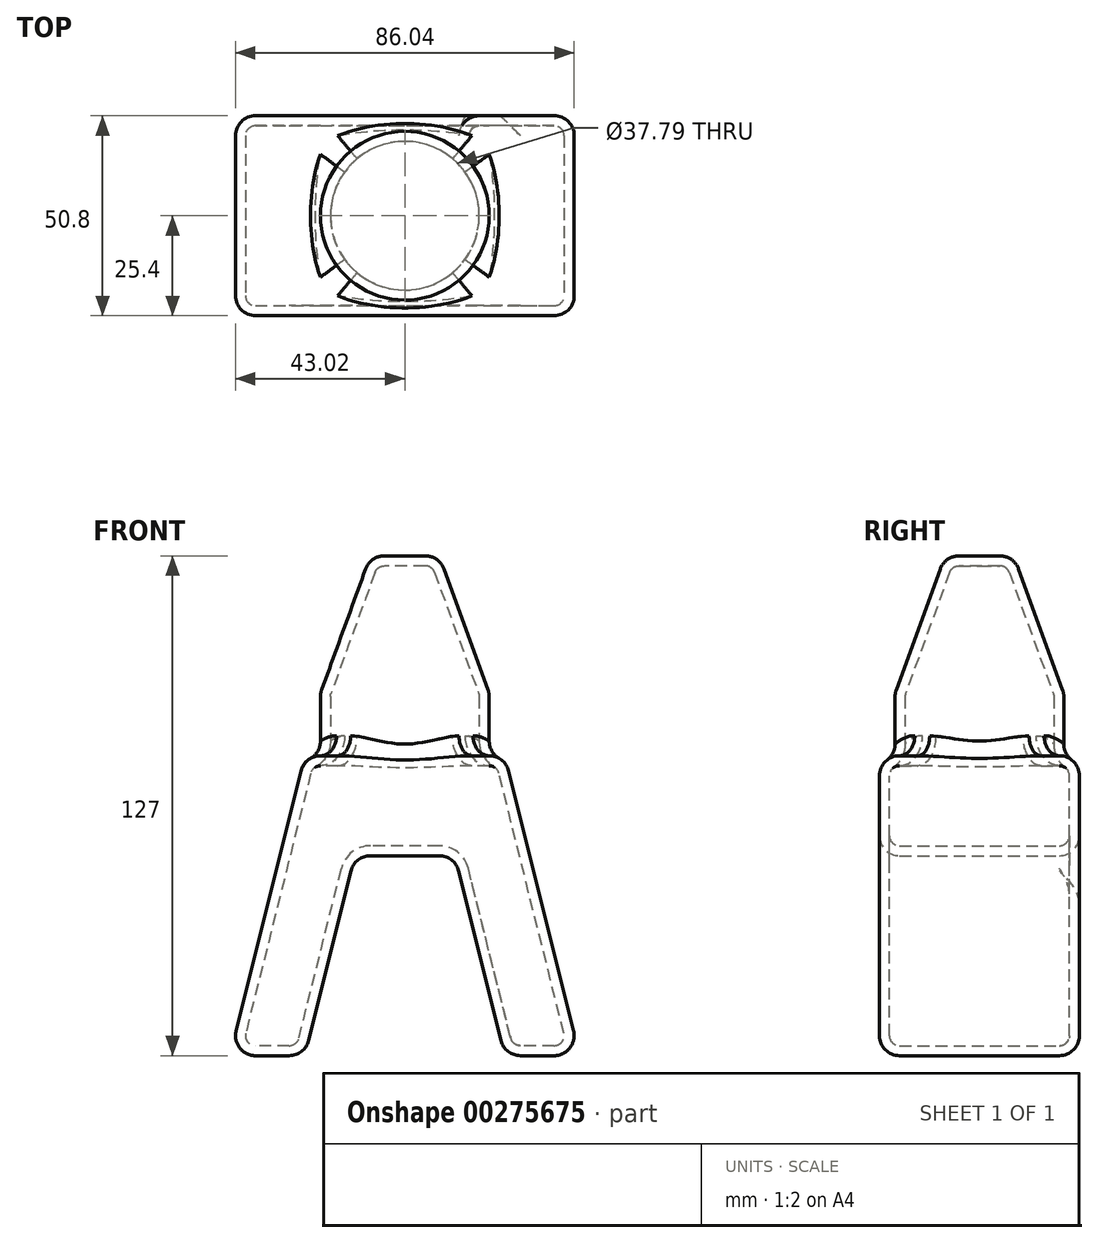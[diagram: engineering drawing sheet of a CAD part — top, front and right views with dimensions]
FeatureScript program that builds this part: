
annotation { "Feature Type Name" : "Feature", "Feature Type Description" : "" }
export const myFeature = defineFeature(function(context is Context, id is Id, definition is map)
    precondition{}
    {
        {
            var Q0;
            Q0=qCreatedBy(makeId("Front.planeOp"),FACE);
            var sketch = newSketch(context, id + "F0", { "sketchPlane" : qUnion([Q0])});
            skLineSegment(sketch, "E0", {"start": v(-25.4, 0) * mm, "end": v(-12.7, 50.8) * mm});
            skLineSegment(sketch, "E1", {"start": v(44.45, 0) * mm, "end": v(25.4, 0) * mm});
            skLineSegment(sketch, "E2", {"start": v(44.45, 0) * mm, "end": v(25.4, 76.2) * mm});
            skLineSegment(sketch, "E3", {"start": v(25.4, 76.2) * mm, "end": v(-25.4, 76.2) * mm});
            skLineSegment(sketch, "E4", {"start": v(-25.4, 76.2) * mm, "end": v(-44.45, 0) * mm});
            skLineSegment(sketch, "E5", {"start": v(-25.4, 0) * mm, "end": v(-44.45, 0) * mm});
            skLineSegment(sketch, "E6", {"start": v(25.4, 0) * mm, "end": v(12.7, 50.8) * mm});
            skLineSegment(sketch, "E7", {"start": v(12.7, 50.8) * mm, "end": v(-12.7, 50.8) * mm});
            skPoint(sketch, "E8", {"position": v(0, 76.2) * mm});
            skPoint(sketch, "E9", {"position": v(0, 50.8) * mm});
            skLineSegment(sketch, "E10", {"start": v(0, 76.2) * mm, "end": v(0, 50.8) * mm, "construction": true});
            skSolve(sketch);
        }
        {
            var Q0;
            Q0 = qSketchRegion(id + "F0", true);
            extrude(context, id + "F1", {"entities" : qUnion([Q0]), "depth" : 25.4 * mm, "hasSecondDirection" : true, "secondDirectionOppositeDirection" : true, "secondDirectionDepth" : 25.4 * mm});
        }
        {
            var Q0;
            Q0=makeQuery(id+"F1.opExtrude","CAP_FACE",FACE,{"disambiguationData":[OSD([sQuery(id+"F0.wireOp",EDGE,"E0"),sQuery(id+"F0.wireOp",EDGE,"E1"),sQuery(id+"F0.wireOp",EDGE,"E2"),sQuery(id+"F0.wireOp",EDGE,"E3"),sQuery(id+"F0.wireOp",EDGE,"E4"),sQuery(id+"F0.wireOp",EDGE,"E5"),sQuery(id+"F0.wireOp",EDGE,"E6"),sQuery(id+"F0.wireOp",EDGE,"E7")])],"isStart":false});
            var Q1;
            Q1=makeQuery(id+"F1.opExtrude","SWEPT_FACE",FACE,{"disambiguationData":[OSD([sQuery(id+"F0.wireOp",EDGE,"E2")])]});
            var Q2;
            Q2=makeQuery(id+"F1.opExtrude","SWEPT_FACE",FACE,{"disambiguationData":[OSD([sQuery(id+"F0.wireOp",EDGE,"E3")])]});
            var Q3;
            Q3=makeQuery(id+"F1.opExtrude","SWEPT_FACE",FACE,{"disambiguationData":[OSD([sQuery(id+"F0.wireOp",EDGE,"E0")])]});
            var Q4;
            Q4=makeQuery(id+"F1.opExtrude","SWEPT_FACE",FACE,{"disambiguationData":[OSD([sQuery(id+"F0.wireOp",EDGE,"E7")])]});
            var Q5;
            Q5=makeQuery(id+"F1.opExtrude","SWEPT_FACE",FACE,{"disambiguationData":[OSD([sQuery(id+"F0.wireOp",EDGE,"E1")])]});
            var Q6;
            Q6=makeQuery(id+"F1.opExtrude","SWEPT_FACE",FACE,{"disambiguationData":[OSD([sQuery(id+"F0.wireOp",EDGE,"E5")])]});
            var Q7;
            Q7=makeQuery(id+"F1.opExtrude","SWEPT_FACE",FACE,{"disambiguationData":[OSD([sQuery(id+"F0.wireOp",EDGE,"E4")])]});
            fillet(context, id + "F2", {"entities" : qUnion([Q0, Q1, Q2, Q3, Q4, Q5, Q6, Q7]), "radius" : 5.08 * mm, "tangentPropagation" : true, "allowEdgeOverflow" : false});
        }
        {
            var Q0;
            Q0=makeQuery(id+"F1.opExtrude","SWEPT_FACE",FACE,{"disambiguationData":[OSD([sQuery(id+"F0.wireOp",EDGE,"E3")])]});
            var sketch = newSketch(context, id + "F3", { "sketchPlane" : qUnion([Q0])});
            skCircle(sketch, "E11", {"center": v(0, 0) * mm, "radius": 21.43 * mm});
            skSolve(sketch);
        }
        {
            var Q0;
            Q0 = qSketchRegion(id + "F3", true);
            extrude(context, id + "F4", {"entities" : qUnion([Q0]), "operationType" : NewBodyOperationType.ADD, "depth" : 50.8 * mm, "hasSecondDirection" : true, "secondDirectionBound" : SecondDirectionBoundingType.UP_TO_NEXT, "secondDirectionOppositeDirection" : true, "secondDirectionDepth" : 25.4 * mm});
        }
        {
            var Q0;
            Q0=makeQuery(id+"F4.opExtrude","CAP_EDGE",EDGE,{"disambiguationData":[OSD([sQuery(id+"F3.wireOp",EDGE,"E11")])],"isStart":false});
            chamfer(context, id + "F5", {"entities" : qUnion([Q0]), "chamferType" : ChamferType.OFFSET_ANGLE, "width" : 12.7 * mm, "oppositeDirection" : false, "angle" : 70 * degree, "tangentPropagation" : true});
        }
        {
            var Q0;
            Q0=makeQuery(id+"F5.opChamfer","BLEND_FACE",FACE,{"disambiguationData":[OSD([sQuery(id+"F3.wireOp",EDGE,"E11")])]});
            var Q1;
            Q1=makeQuery(id+"F4.opExtrude","SWEPT_FACE",FACE,{"disambiguationData":[OSD([sQuery(id+"F3.wireOp",EDGE,"E11")])]});
            fillet(context, id + "F6", {"entities" : qUnion([Q0, Q1]), "radius" : 5.08 * mm, "tangentPropagation" : true, "allowEdgeOverflow" : false});
        }
        {
            var Q0;
            Q0=makeQuery(id+"F5.opChamfer","BLEND_FACE",FACE,{"disambiguationData":[OSD([sQuery(id+"F3.wireOp",EDGE,"E11")])]});
            var Q1;
            Q1=makeQuery(id+"F1.opExtrude","CAP_FACE",FACE,{"disambiguationData":[OSD([sQuery(id+"F0.wireOp",EDGE,"E0"),sQuery(id+"F0.wireOp",EDGE,"E1"),sQuery(id+"F0.wireOp",EDGE,"E2"),sQuery(id+"F0.wireOp",EDGE,"E3"),sQuery(id+"F0.wireOp",EDGE,"E4"),sQuery(id+"F0.wireOp",EDGE,"E5"),sQuery(id+"F0.wireOp",EDGE,"E6"),sQuery(id+"F0.wireOp",EDGE,"E7")])],"isStart":true});
            var Q2;
            Q2=makeQuery(id+"F1.opExtrude","SWEPT_FACE",FACE,{"disambiguationData":[OSD([sQuery(id+"F0.wireOp",EDGE,"E2")])]});
            var Q3;
            Q3=makeQuery(id+"F1.opExtrude","CAP_FACE",FACE,{"disambiguationData":[OSD([sQuery(id+"F0.wireOp",EDGE,"E0"),sQuery(id+"F0.wireOp",EDGE,"E1"),sQuery(id+"F0.wireOp",EDGE,"E2"),sQuery(id+"F0.wireOp",EDGE,"E3"),sQuery(id+"F0.wireOp",EDGE,"E4"),sQuery(id+"F0.wireOp",EDGE,"E5"),sQuery(id+"F0.wireOp",EDGE,"E6"),sQuery(id+"F0.wireOp",EDGE,"E7")])],"isStart":false});
            var Q4;
            Q4=makeQuery(id+"F1.opExtrude","SWEPT_BODY",BODY,{"disambiguationData":[OSD([sQuery(id+"F0.wireOp",EDGE,"E0"),sQuery(id+"F0.wireOp",EDGE,"E1"),sQuery(id+"F0.wireOp",EDGE,"E2"),sQuery(id+"F0.wireOp",EDGE,"E3"),sQuery(id+"F0.wireOp",EDGE,"E4"),sQuery(id+"F0.wireOp",EDGE,"E5"),sQuery(id+"F0.wireOp",EDGE,"E6"),sQuery(id+"F0.wireOp",EDGE,"E7")])]});
            shell(context, id + "F7", {"isHollow" : true, "entities" : qUnion([Q0, Q1, Q2, Q3]), "parts" : qUnion([Q4]), "thickness" : 2.54 * mm});
        }
    });
